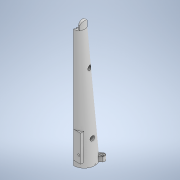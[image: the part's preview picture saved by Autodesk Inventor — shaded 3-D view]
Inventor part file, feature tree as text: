
AUTODESK INVENTOR PART (.ipt)
format: ipt  version: 2021 (Build 250183000, 183)  size: 1,108,992 bytes
history: native  units: mm
features: sketch x40, extrude x38, plane x17, fillet x9, hole x3, thread x3, loft x2, revolve x2, other x1
ambient origin geometry x8: Origin, YZ Plane, XZ Plane, XY Plane, X Axis, Y Axis, Z Axis, Center Point
bodies: Body1 (feature_tree)
feature tree (115):
  other  "Sólido1"
  plane  "Plano de trabajo1"
  plane  "Plano de trabajo2"
  plane  "Plano de trabajo4"
  plane  "Plano de trabajo5"
  plane  "Plano de trabajo6"
  sketch  "Boceto1"  dims[d1=250.0mm d2=0.0mm d3=-80.0mm d4=-110.0mm]
  sketch  "Boceto2"  dims[d5=-140.0mm d7=-0.0mm d8=2.0mm]
  sketch  "Boceto3"  dims[d9=140.0mm d10=250.0mm]
  sketch  "Boceto4"  dims[d11=24.0mm d22=0.0mm d23=90.0deg d24=0.0mm d25=90.0deg]
  sketch  "Boceto6"  dims[d44=45.0mm d49=29.11157mm]
  sketch  "Boceto7"  dims[d50=29.11157mm d53=29.11157mm]
  loft  "Solevación1"
  fillet  "Empalme2"  [1 undecoded]
  extrude  "Extrusión1"  TaperAngle=0.0deg  [1 undecoded]
  fillet  "Empalme5"  Radius=2.0mm
  plane  "Plano de trabajo7"
  extrude  "Extrusión2"  Depth=250.0mm
  plane  "Plano de trabajo8"
  plane  "Plano de trabajo9"
  loft  "Solevación9"
  plane  "Plano de trabajo10"
  extrude  "Extrusión3"  Depth=29.11157mm
  plane  "Plano de trabajo11"
  revolve  "Revolución1"  [1 undecoded]
  revolve  "Revolución2"  [1 undecoded]
  extrude  "Extrusión4"  Depth=32.5mm
  plane  "Plano de trabajo12"
  extrude  "Extrusión5"  Depth=44.747934mm
  plane  "Plano de trabajo13"
  plane  "Plano de trabajo14"
  extrude  "Extrusión6"  Depth=42.747934mm
  extrude  "Extrusión7"  Depth=42.747934mm
  extrude  "Extrusión8"  Depth=13.0mm
  extrude  "Extrusión11"  Depth=6.5mm
  extrude  "Extrusión9"  Depth=7.75mm
  extrude  "Extrusión10"  Depth=16.0mm
  extrude  "Extrusión12"  Depth=12.0mm
  sketch  "Boceto30"  dims[d160=-19.75mm d161=0.0mm]
  extrude  "Extrusión13"  Depth=7.75mm
  extrude  "Extrusión14"  Depth=6.5mm
  extrude  "Extrusión15"  TaperAngle=0.0deg  [1 undecoded]
  hole  "Agujero1"  [1 undecoded]
  thread  "Rosca1"  [1 undecoded]
  extrude  "Extrusión16"  Depth=2.0mm
  plane  "Plano de trabajo16"
  extrude  "Extrusión17"  TaperAngle=0.0deg  [1 undecoded]
  extrude  "Extrusión18"  TaperAngle=0.0deg  [1 undecoded]
  plane  "Plano de trabajo17"
  sketch  "Boceto46"  dims[d185=2.0mm d187=1.0mm]
  hole  "Agujero2"  [1 undecoded]
  hole  "Agujero3"  [1 undecoded]
  plane  "Plano de trabajo19"
  sketch  "Boceto50"  dims[d193=0.25mm d194=90.0deg]
  extrude  "Extrusión22"  Depth=12.0mm
  extrude  "Extrusión23"  [1 undecoded]
  extrude  "Extrusión24"  Depth=0.75mm
  plane  "Plano de trabajo20"
  extrude  "Extrusión25"  Depth=1.0mm
  fillet  "Empalme6"  Radius=11.0mm
  fillet  "Empalme7"  Radius=17.453293mm
  sketch  "Boceto49"  dims[d191=2.0mm d192=0.25mm]
  extrude  "Extrusión29"  Depth=0.75mm
  extrude  "Extrusión30"  Depth=0.25mm
  sketch  "Boceto44"  dims[d181=0.75mm d182=0.25mm]
  sketch  "Boceto47"  dims[d189=3.0mm d190=2.0mm]
  extrude  "Extrusión26"  Depth=0.25mm
  extrude  "Extrusión27"  Depth=2.0mm
  extrude  "Extrusión28"  Depth=2.0mm
  sketch  "Boceto45"  dims[d183=1.0mm d184=0.25mm]
  extrude  "Extrusión31"  Depth=2.0mm
  extrude  "Extrusión32"  TaperAngle=90.0deg  [1 undecoded]
  extrude  "Extrusión33"  [1 undecoded]
  extrude  "Extrusión34"  Depth=20.0mm
  extrude  "Extrusión35"  Depth=2.0mm
  thread  "Rosca2"  [1 undecoded]
  thread  "Rosca3"  [1 undecoded]
  fillet  "Empalme8"  [1 undecoded]
  fillet  "Empalme9"  Radius=0.5mm
  fillet  "Empalme10"  Radius=0.25mm
  fillet  "Empalme11"  [1 undecoded]
  extrude  "Extrusión36"  Depth=1.8mm TaperAngle=0.0deg
  extrude  "Extrusión37"  Depth=1.8mm TaperAngle=0.0deg
  fillet  "Empalme12"  Radius=2.0mm
  sketch  "Boceto54"  dims[d201=9.0mm d202=9.0mm d203=2.0mm d204=201.65mm d205=0.0mm d206=0.5mm d207=0.25mm d208=-7.5mm]
  extrude  "Agujero_tornillo_caja"  Depth=1.8mm
  extrude  "Extrusión40"  Depth=6.5mm
  extrude  "Test_section"  Depth=1.8mm
  extrude  "Extrusión41"  Depth=1.8mm
  sketch  "Boceto55"  dims[d209=100.0mm d210=0.0mm d211=35.0mm d212=0.0mm d213=210.0mm d214=0.0mm d215=2.0mm d216=1.059493mm d217=6.5mm d218=1.059493mm d219=5.0mm d220=2.0mm d221=0.0mm d222=2.0mm d223=6.5mm d224=1.059493mm d225=5.0mm d226=4.85mm d227=2.0mm d228=0.0mm d229=6.0mm d230=10.0mm d231=3.0mm d232=11.0mm d233=10.5mm d235=30.0deg d236=4.75mm d237=0.0mm d238=-17.0mm d239=100.0mm d240=0.0mm d241=6.5mm d242=1.65mm d243=3.3mm d244=15.6mm d245=2.0mm d247=16.0mm d248=2.0mm d249=0.0mm d250=4.5mm d251=0.75mm d252=2.5mm d253=1.0mm d254=11.0mm d255=17.453293mm d256=2.939597mm d257=0.75mm d258=0.75mm d259=0.25mm d260=1.0mm d261=0.25mm d262=2.0mm d263=1.0mm d264=3.0mm d265=2.0mm d266=2.0mm d267=0.25mm d268=0.25mm d269=40.0mm d270=1.0mm d271=1.0mm d272=7.75mm d273=0.5mm d274=8.5mm d275=90.0deg d276=0.0mm d277=17.75mm d280=22.5mm d281=2.0mm d282=0.0mm d283=0.0mm d292=2.0mm d293=0.0mm d296=3.5mm d297=0.0mm d299=4.0mm d300=3.708mm d301=3.023mm d302=2.0mm d303=14.3117mm d304=16.0mm d305=0.0mm d306=16.0mm d307=0.0mm d314=6.0mm d315=19.2mm d316=6.0mm d317=19.2mm d318=13.0mm d320=6.0mm d321=19.2mm d322=13.0mm d323=6.0mm d324=19.2mm d325=13.0mm d326=7.0mm d332=10.0mm d333=0.0mm d335=-41.6mm d336=4.0mm d337=1.0mm d338=9.0mm d339=4.0mm d340=1.0mm d341=9.0mm d342=4.0mm d343=5.2mm d344=6.0mm d345=0.0mm d346=15.0mm d347=5.0mm d349=5.0mm d351=0.0mm d352=45.0mm d354=10.0mm d355=10.0mm d356=0.0mm d357=15.0mm d358=0.0mm d359=2.0mm d363=50.4125mm d376=14.059493mm d377=2.0mm d378=0.0mm d379=2.0mm d380=11.25mm d381=90.0mm d382=290.0mm d383=14.059493mm d384=100.825mm d390=30.940507mm d391=2.0mm d392=100.825mm d393=14.790546mm d394=2.0mm d395=3.0mm d396=6.0mm d397=4.0mm d398=4.0mm d399=4.0mm d400=8.128453mm d401=12.0mm d402=4.45mm d403=2.5mm d404=1.65mm d405=1.65mm d406=1.0mm d407=2.0mm d408=2.0mm d409=0.0mm d411=50.4125mm d412=6.0mm d418=13.059493mm d419=6.5mm d420=6.5mm d421=50.4125mm d422=126.03125mm d423=0.0mm d424=15.0mm d425=5.0mm d426=5.0mm d427=0.0mm d428=45.0mm d429=10.0mm d430=2.0mm d431=4.0mm d432=6.0mm d433=8.0mm d434=2.0mm d435=90.0deg d436=20.0mm d437=0.0mm d438=4.0mm d439=6.0mm d440=8.0mm d441=2.0mm d442=90.0deg d443=20.0mm d444=0.0mm d446=10.0mm d447=3.0mm d448=11.0mm d450=9.2mm d451=9.2mm d452=90.0mm d453=750.0mm d454=22.5mm d455=43.0mm d456=44.0mm d457=14.059493mm d458=11.25mm d461=22.5mm d462=43.0mm d463=7.059493mm d464=3.0mm d465=6.0mm d466=3.0mm d467=6.0mm d468=45.0mm d469=67.0mm d470=19.686mm d471=30.0mm d472=15.0mm d473=0.0mm d474=1.5mm d475=2.0mm d476=1.5mm d477=2.0mm d478=57.0mm d479=0.0mm d480=57.0mm d481=0.0mm d482=53.0mm d483=0.0mm d484=37.0mm d485=0.0mm d486=-1.5mm d487=33.895511mm d488=2.6mm d489=60.0deg d490=45.0deg d491=15.0mm d492=1.6mm d493=0.0mm d494=180.0mm d495=0.0mm d496=180.0mm d497=0.0mm d498=2.0mm d499=0.0mm d500=4.1mm d501=4.4mm d502=10.0mm d503=0.0mm d504=7.0mm d505=0.0mm d506=7.0mm d507=0.0mm d508=4.4mm d509=4.4mm d510=4.4mm d511=7.0mm d512=0.0mm d513=25.497mm d514=0.0mm d515=0.0mm d516=0.0mm d517=4.0mm d518=4.0mm d519=2.0mm d520=0.0mm d521=2.0mm d522=0.0mm d523=2.0mm d524=0.0mm d525=1.0mm d526=0.8mm d527=1.0mm d528=0.8mm d533=3.0mm d534=1.5mm d537=1.0mm d538=6.5mm d539=3.0mm d540=1.5mm d541=0.0mm d542=0.0mm d543=2.0mm d544=0.0mm d545=2.5mm d546=135.0mm d547=4.0mm d548=67.0mm d549=0.0mm d550=0.0mm d551=25.0mm d552=11.0mm d553=4.0mm d554=6.0mm d555=12.0mm d556=0.0mm d557=10.0mm d558=0.0mm d559=1.2mm d560=1.8mm d561=0.0mm]
  sketch  "Boceto9"  dims[d59=29.11157mm d61=29.11157mm]
  sketch  "Boceto10"  dims[d65=22.5mm d66=32.5mm]
  sketch  "Boceto15"  dims[d67=22.5mm d90=44.747934mm]
  sketch  "Boceto16"  dims[d91=42.747934mm d93=42.747934mm]
  sketch  "Boceto17"  dims[d96=0.0mm d97=90.0deg d98=0.0mm d99=90.0deg d100=0.0mm d101=90.0deg d102=0.0mm d103=90.0deg d112=42.747934mm]
  sketch  "Boceto18"  dims[d115=5.0mm d120=13.0mm]
  sketch  "Boceto19"  dims[d121=6.5mm d124=7.75mm]
  sketch  "Boceto20"  dims[d125=7.75mm d126=7.75mm]
  sketch  "Boceto21"  dims[d127=7.75mm d130=16.0mm]
  sketch  "Boceto22"  dims[d131=0.0mm d132=12.0mm]
  sketch  "Boceto24"  dims[d133=12.0mm d134=7.75mm]
  sketch  "Boceto25"  dims[d135=6.5mm d136=7.75mm]
  sketch  "Boceto26"  dims[d137=15.0mm d138=0.0mm]
  sketch  "Boceto27"  dims[d146=-8.5mm d147=30.0mm d148=2.0mm]
  sketch  "Boceto28"  dims[d149=25.12mm d150=2.0mm]
  sketch  "Boceto29"  dims[d151=10.357mm d156=0.0mm d157=90.0deg d158=0.0mm d159=90.0deg]
  sketch  "Boceto31"  dims[d163=0.0mm d164=2.0mm]
  sketch  "Boceto36"  dims[d165=15.0mm d166=4.0mm]
  sketch  "Boceto37"  dims[d167=30.0mm d168=12.0mm]
  sketch  "Boceto38"  dims[d169=0.0mm d170=-7.25mm]
  sketch  "Boceto39"  dims[d171=4.5mm d172=0.75mm]
  sketch  "Boceto40"  dims[d173=2.5mm d174=1.0mm d176=11.0mm d177=17.453293mm]
  sketch  "Boceto41"  dims[d179=2.939597mm d180=0.75mm]
  sketch  "Boceto51"  dims[d196=4.381635mm d197=0.0mm d198=-48.35mm]
  sketch  "Boceto53"  dims[d199=12.0mm d200=20.0mm]
note: 18 required parameter values undecoded (feature->parameter linkage not recoverable at this tier; creation-order binding heuristic only, values carry confidence <= 0.55)